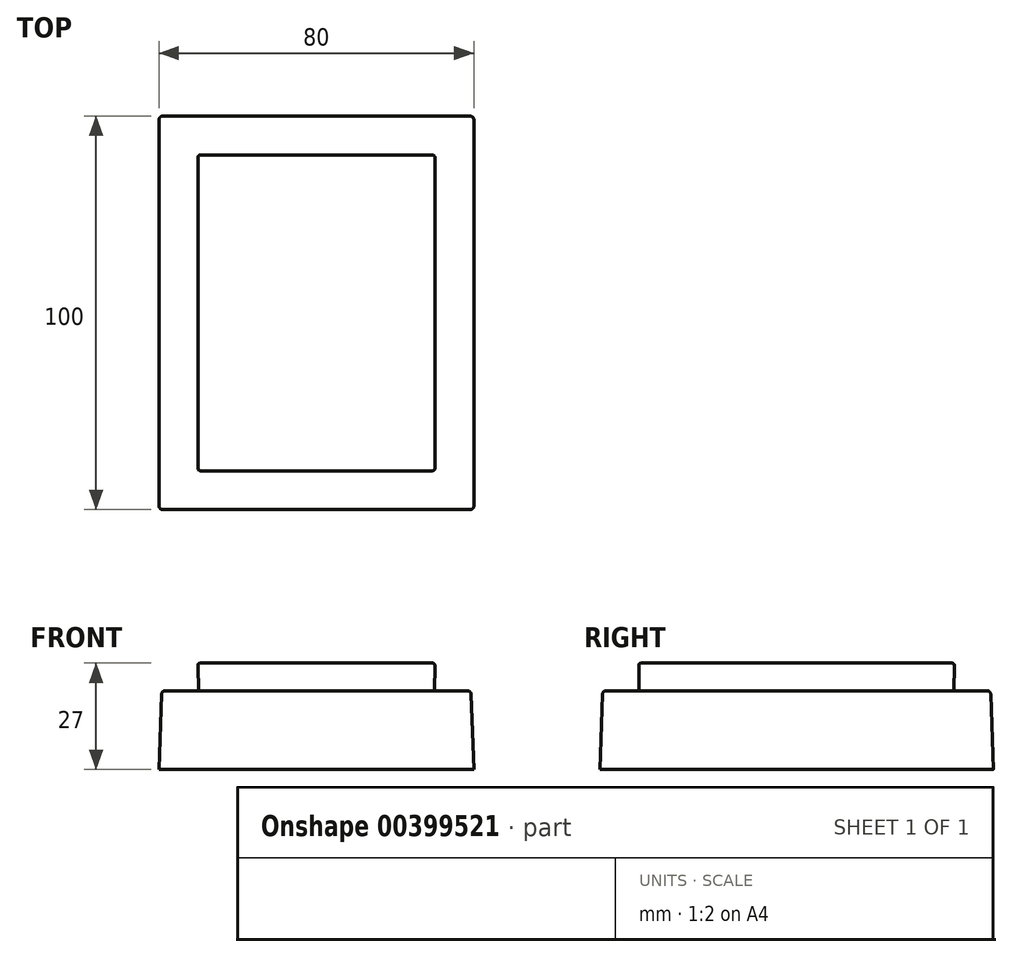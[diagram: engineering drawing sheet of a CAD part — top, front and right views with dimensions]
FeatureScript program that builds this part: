
annotation { "Feature Type Name" : "Feature", "Feature Type Description" : "" }
export const myFeature = defineFeature(function(context is Context, id is Id, definition is map)
    precondition{}
    {
        {
            var Q0;
            Q0=qCreatedBy(makeId("Top.planeOp"),FACE);
            var sketch = newSketch(context, id + "F0", { "sketchPlane" : qUnion([Q0])});
            skLineSegment(sketch, "E0.bottom", {"start": v(40, 50) * mm, "end": v(-40, 50) * mm});
            skLineSegment(sketch, "E0.top", {"start": v(40, -50) * mm, "end": v(-40, -50) * mm});
            skLineSegment(sketch, "E0.left", {"start": v(40, 50) * mm, "end": v(40, -50) * mm});
            skLineSegment(sketch, "E0.right", {"start": v(-40, 50) * mm, "end": v(-40, -50) * mm});
            skPoint(sketch, "E0.middle", {"position": v(0, 0) * mm});
            skSolve(sketch);
        }
        {
            var Q0;
            Q0 = qSketchRegion(id + "F0", true);
            extrude(context, id + "F1", {"entities" : qUnion([Q0]), "depth" : 20 * mm, "hasDraft" : true, "draftAngle" : 2 * degree, "draftPullDirection" : true});
        }
        {
            var Q0;
            Q0=makeQuery(id+"F1.opExtrude","CAP_FACE",FACE,{"disambiguationData":[OSD([sQuery(id+"F0.wireOp",EDGE,"E0.bottom"),sQuery(id+"F0.wireOp",EDGE,"E0.top"),sQuery(id+"F0.wireOp",EDGE,"E0.left"),sQuery(id+"F0.wireOp",EDGE,"E0.right")])],"isStart":false});
            var sketch = newSketch(context, id + "F2", { "sketchPlane" : qUnion([Q0])});
            skLineSegment(sketch, "E1.bottom", {"start": v(30, 40) * mm, "end": v(-30, 40) * mm});
            skLineSegment(sketch, "E1.top", {"start": v(30, -40) * mm, "end": v(-30, -40) * mm});
            skLineSegment(sketch, "E1.left", {"start": v(30, 40) * mm, "end": v(30, -40) * mm});
            skLineSegment(sketch, "E1.right", {"start": v(-30, 40) * mm, "end": v(-30, -40) * mm});
            skPoint(sketch, "E1.middle", {"position": v(0, 0) * mm});
            skSolve(sketch);
        }
        {
            var Q0;
            Q0 = qSketchRegion(id + "F2", true);
            extrude(context, id + "F3", {"entities" : qUnion([Q0]), "operationType" : NewBodyOperationType.ADD, "depth" : 7 * mm, "hasDraft" : true, "draftAngle" : 1 * degree});
        }
        {
            var Q0;
            Q0=makeQuery(id+"F1.opExtrude","SWEPT_EDGE",EDGE,{"disambiguationData":[OSD([sQuery(id+"F0.wireOp",EDGE,"E0.bottom"),sQuery(id+"F0.wireOp",EDGE,"E0.right")])]});
            var Q1;
            Q1=makeQuery(id+"F1.opExtrude","SWEPT_EDGE",EDGE,{"disambiguationData":[OSD([sQuery(id+"F0.wireOp",EDGE,"E0.bottom"),sQuery(id+"F0.wireOp",EDGE,"E0.left")])]});
            var Q2;
            Q2=makeQuery(id+"F1.opExtrude","SWEPT_EDGE",EDGE,{"disambiguationData":[OSD([sQuery(id+"F0.wireOp",EDGE,"E0.top"),sQuery(id+"F0.wireOp",EDGE,"E0.left")])]});
            var Q3;
            Q3=makeQuery(id+"F1.opExtrude","SWEPT_EDGE",EDGE,{"disambiguationData":[OSD([sQuery(id+"F0.wireOp",EDGE,"E0.top"),sQuery(id+"F0.wireOp",EDGE,"E0.right")])]});
            var Q4;
            Q4=makeQuery(id+"F1.opExtrude","CAP_EDGE",EDGE,{"disambiguationData":[OSD([sQuery(id+"F0.wireOp",EDGE,"E0.bottom")])],"isStart":false});
            var Q5;
            Q5=makeQuery(id+"F1.opExtrude","CAP_EDGE",EDGE,{"disambiguationData":[OSD([sQuery(id+"F0.wireOp",EDGE,"E0.right")])],"isStart":false});
            var Q6;
            Q6=makeQuery(id+"F1.opExtrude","CAP_EDGE",EDGE,{"disambiguationData":[OSD([sQuery(id+"F0.wireOp",EDGE,"E0.top")])],"isStart":false});
            var Q7;
            Q7=makeQuery(id+"F1.opExtrude","CAP_EDGE",EDGE,{"disambiguationData":[OSD([sQuery(id+"F0.wireOp",EDGE,"E0.left")])],"isStart":false});
            fillet(context, id + "F4", {"entities" : qUnion([Q0, Q1, Q2, Q3, Q4, Q5, Q6, Q7]), "radius" : 1 * mm, "tangentPropagation" : true, "allowEdgeOverflow" : false});
        }
        {
            var Q0;
            Q0=makeQuery(id+"F3.opExtrude","SWEPT_EDGE",EDGE,{"disambiguationData":[OSD([sQuery(id+"F2.wireOp",EDGE,"E1.bottom"),sQuery(id+"F2.wireOp",EDGE,"E1.right")])]});
            var Q1;
            Q1=makeQuery(id+"F3.opExtrude","CAP_EDGE",EDGE,{"disambiguationData":[OSD([sQuery(id+"F2.wireOp",EDGE,"E1.right")])],"isStart":false});
            var Q2;
            Q2=makeQuery(id+"F3.opExtrude","CAP_EDGE",EDGE,{"disambiguationData":[OSD([sQuery(id+"F2.wireOp",EDGE,"E1.bottom")])],"isStart":false});
            var Q3;
            Q3=makeQuery(id+"F3.opExtrude","SWEPT_EDGE",EDGE,{"disambiguationData":[OSD([sQuery(id+"F2.wireOp",EDGE,"E1.bottom"),sQuery(id+"F2.wireOp",EDGE,"E1.left")])]});
            var Q4;
            Q4=makeQuery(id+"F3.opExtrude","CAP_EDGE",EDGE,{"disambiguationData":[OSD([sQuery(id+"F2.wireOp",EDGE,"E1.left")])],"isStart":false});
            var Q5;
            Q5=makeQuery(id+"F3.opExtrude","SWEPT_EDGE",EDGE,{"disambiguationData":[OSD([sQuery(id+"F2.wireOp",EDGE,"E1.top"),sQuery(id+"F2.wireOp",EDGE,"E1.left")])]});
            var Q6;
            Q6=makeQuery(id+"F3.opExtrude","CAP_EDGE",EDGE,{"disambiguationData":[OSD([sQuery(id+"F2.wireOp",EDGE,"E1.top")])],"isStart":false});
            var Q7;
            Q7=makeQuery(id+"F3.opExtrude","SWEPT_EDGE",EDGE,{"disambiguationData":[OSD([sQuery(id+"F2.wireOp",EDGE,"E1.top"),sQuery(id+"F2.wireOp",EDGE,"E1.right")])]});
            fillet(context, id + "F5", {"entities" : qUnion([Q0, Q1, Q2, Q3, Q4, Q5, Q6, Q7]), "radius" : .6 * mm, "tangentPropagation" : true, "allowEdgeOverflow" : false});
        }
    });
